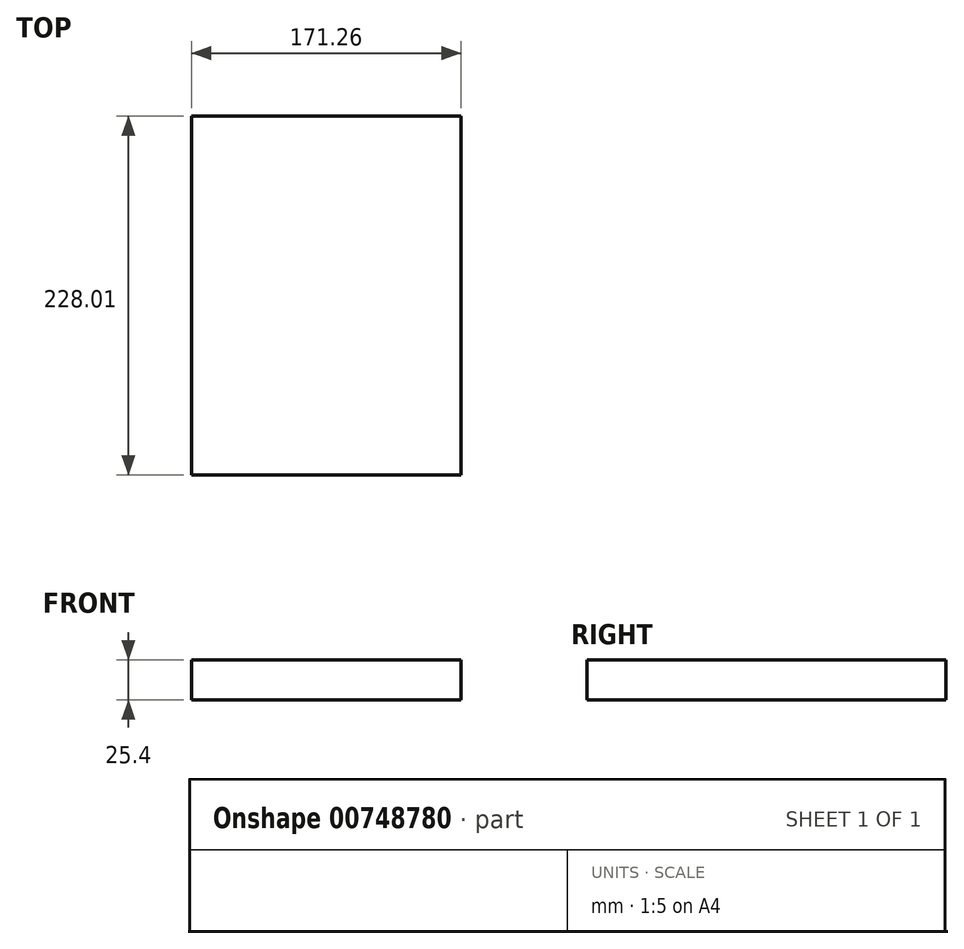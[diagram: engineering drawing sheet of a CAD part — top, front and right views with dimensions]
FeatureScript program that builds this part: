
annotation { "Feature Type Name" : "Feature", "Feature Type Description" : "" }
export const myFeature = defineFeature(function(context is Context, id is Id, definition is map)
    precondition{}
    {
        {
            var Q0;
            Q0=qCreatedBy(makeId("Top.planeOp"),FACE);
            var sketch = newSketch(context, id + "F0", { "sketchPlane" : qUnion([Q0])});
            skLineSegment(sketch, "E0.bottom", {"start": v(-74.08, -73.44) * mm, "end": v(97.18, -73.44) * mm});
            skLineSegment(sketch, "E0.top", {"start": v(-74.08, 154.57) * mm, "end": v(97.18, 154.57) * mm});
            skLineSegment(sketch, "E0.left", {"start": v(-74.08, -73.44) * mm, "end": v(-74.08, 154.57) * mm});
            skLineSegment(sketch, "E0.right", {"start": v(97.18, -73.44) * mm, "end": v(97.18, 154.57) * mm});
            skSolve(sketch);
        }
        {
            var Q0;
            Q0 = qSketchRegion(id + "F0", true);
            extrude(context, id + "F1", {"entities" : qUnion([Q0]), "depth" : 25.4 * mm, "offsetDistance" : 25.4 * mm});
        }
    });
